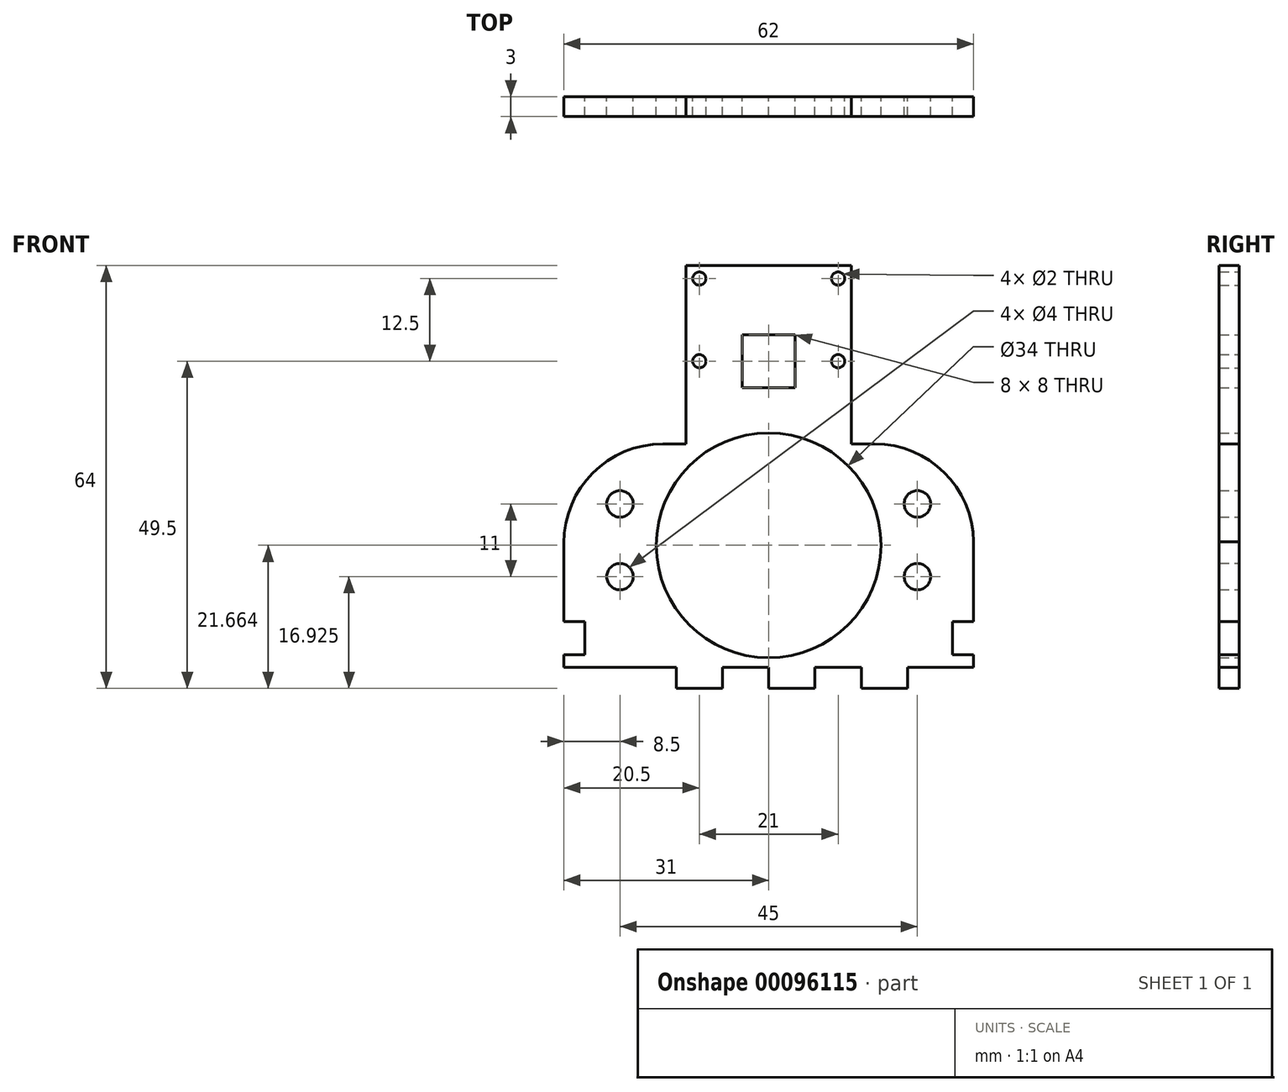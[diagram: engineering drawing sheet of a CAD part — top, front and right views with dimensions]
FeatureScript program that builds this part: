
annotation { "Feature Type Name" : "Feature", "Feature Type Description" : "" }
export const myFeature = defineFeature(function(context is Context, id is Id, definition is map)
    precondition{}
    {
        {
            var Q0;
            Q0=qCreatedBy(makeId("Front.planeOp"),FACE);
            var sketch = newSketch(context, id + "F0", { "sketchPlane" : qUnion([Q0])});
            skLineSegment(sketch, "E0.bottom", {"start": v(12.5, 13.5) * mm, "end": v(-12.5, 13.5) * mm});
            skLineSegment(sketch, "E0.left", {"start": v(12.5, 13.5) * mm, "end": v(12.5, -13.5) * mm});
            skLineSegment(sketch, "E0.right", {"start": v(-12.5, 13.5) * mm, "end": v(-12.5, -13.5) * mm});
            skPoint(sketch, "E0.middle", {"position": v(0, 0) * mm});
            skLineSegment(sketch, "E1", {"start": v(0, 13.5) * mm, "end": v(0, -1) * mm, "construction": true});
            skPoint(sketch, "E1.endSnap0", {"position": v(0, 13.5) * mm});
            skLineSegment(sketch, "E2.bottom", {"start": v(4, 3) * mm, "end": v(-4, 3) * mm});
            skLineSegment(sketch, "E2.top", {"start": v(4, -5) * mm, "end": v(-4, -5) * mm});
            skLineSegment(sketch, "E2.left", {"start": v(4, 3) * mm, "end": v(4, -5) * mm});
            skLineSegment(sketch, "E2.right", {"start": v(-4, 3) * mm, "end": v(-4, -5) * mm});
            skPoint(sketch, "E2.middle", {"position": v(0, -1) * mm});
            skCircle(sketch, "E3", {"center": v(-10.5, 11.5) * mm, "radius": 1 * mm});
            skCircle(sketch, "E4", {"center": v(-10.5, -1) * mm, "radius": 1 * mm});
            skPoint(sketch, "E4.centerSnap0", {"position": v(-4, -1) * mm});
            skCircle(sketch, "E5.MirrorC", {"center": v(10.5, 11.5) * mm, "radius": 1 * mm});
            skCircle(sketch, "E6.MirrorC", {"center": v(10.5, -1) * mm, "radius": 1 * mm});
            skCircle(sketch, "E7", {"center": v(0, -28.84) * mm, "radius": 17 * mm});
            skLineSegment(sketch, "E8", {"start": v(-12.5, -13.5) * mm, "end": v(-16, -13.5) * mm});
            skLineSegment(sketch, "E9", {"start": v(12.5, -13.5) * mm, "end": v(16, -13.5) * mm});
            skArc(sketch, "E10.filletArc", {"start": v(-16, -13.5) * mm, "mid": v(-26.6, -17.9) * mm, "end": v(-31, -28.5) * mm});
            skArc(sketch, "E11.filletArc", {"start": v(31, -28.3) * mm, "mid": v(26.54, -17.82) * mm, "end": v(16, -13.5) * mm});
            skPoint(sketch, "E12.MirrorCS.start.orphan", {"position": v(0, -45.84) * mm});
            skLineSegment(sketch, "E13", {"start": v(-31, -28.5) * mm, "end": v(-31, -35.5) * mm});
            skLineSegment(sketch, "E14", {"start": v(31, -28.3) * mm, "end": v(31, -30.3) * mm});
            skLineSegment(sketch, "E15", {"start": v(0, -28.84) * mm, "end": v(0, -13.5) * mm, "construction": true});
            skLineSegment(sketch, "E16", {"start": v(-31, -30.3) * mm, "end": v(31, -30.3) * mm, "construction": true});
            skLineSegment(sketch, "E17", {"start": v(31, -30.3) * mm, "end": v(31, -35.5) * mm});
            skLineSegment(sketch, "E18", {"start": v(-28, -40.5) * mm, "end": v(28, -40.5) * mm, "construction": true});
            skLineSegment(sketch, "E19", {"start": v(-28, -35.5) * mm, "end": v(28, -35.5) * mm, "construction": true});
            skLineSegment(sketch, "E20", {"start": v(-28, -45.5) * mm, "end": v(28, -45.5) * mm, "construction": true});
            skLineSegment(sketch, "E21.trimOffspring", {"start": v(-31, -35.5) * mm, "end": v(-31, -30.3) * mm, "construction": true});
            skLineSegment(sketch, "E22", {"start": v(31, -47.3) * mm, "end": v(31, -45.4) * mm, "construction": true});
            skLineSegment(sketch, "E23", {"start": v(31, -45.4) * mm, "end": v(27.8, -45.4) * mm});
            skLineSegment(sketch, "E24", {"start": v(27.8, -45.4) * mm, "end": v(27.8, -40.4) * mm});
            skLineSegment(sketch, "E25", {"start": v(27.8, -40.4) * mm, "end": v(31, -40.4) * mm});
            skLineSegment(sketch, "E26", {"start": v(31, -40.4) * mm, "end": v(31, -35.5) * mm});
            skLineSegment(sketch, "E27", {"start": v(-31, -47.3) * mm, "end": v(-31, -45.4) * mm});
            skLineSegment(sketch, "E28", {"start": v(-31, -45.4) * mm, "end": v(-27.8, -45.4) * mm});
            skLineSegment(sketch, "E29", {"start": v(-27.8, -45.4) * mm, "end": v(-27.8, -40.4) * mm});
            skLineSegment(sketch, "E30", {"start": v(-27.8, -40.4) * mm, "end": v(-31, -40.4) * mm});
            skLineSegment(sketch, "E31", {"start": v(-31, -40.4) * mm, "end": v(-31, -35.5) * mm});
            skLineSegment(sketch, "E32", {"start": v(31, -45.4) * mm, "end": v(31, -47.3) * mm});
            skLineSegment(sketch, "E33", {"start": v(0, -22.57) * mm, "end": v(-22.5, -22.57) * mm, "construction": true});
            skLineSegment(sketch, "E34", {"start": v(0, -22.57) * mm, "end": v(22.5, -22.57) * mm, "construction": true});
            skCircle(sketch, "E35", {"center": v(-22.5, -22.57) * mm, "radius": 2 * mm});
            skCircle(sketch, "E36", {"center": v(22.5, -22.57) * mm, "radius": 2 * mm});
            skLineSegment(sketch, "E37", {"start": v(-22.5, -22.57) * mm, "end": v(-22.5, -33.57) * mm, "construction": true});
            skLineSegment(sketch, "E38", {"start": v(22.5, -22.57) * mm, "end": v(22.5, -33.57) * mm, "construction": true});
            skCircle(sketch, "E39", {"center": v(-22.5, -33.57) * mm, "radius": 2 * mm});
            skCircle(sketch, "E40", {"center": v(22.5, -33.57) * mm, "radius": 2 * mm});
            skLineSegment(sketch, "E41", {"start": v(-31, -47.3) * mm, "end": v(-14, -47.3) * mm});
            skLineSegment(sketch, "E42", {"start": v(-14, -47.3) * mm, "end": v(-14, -50.5) * mm});
            skLineSegment(sketch, "E43", {"start": v(-14, -50.5) * mm, "end": v(-7, -50.5) * mm});
            skLineSegment(sketch, "E44", {"start": v(-7, -50.5) * mm, "end": v(-7, -47.3) * mm});
            skLineSegment(sketch, "E45", {"start": v(-7, -47.3) * mm, "end": v(0, -47.3) * mm});
            skLineSegment(sketch, "E46", {"start": v(0, -47.3) * mm, "end": v(0, -50.5) * mm});
            skLineSegment(sketch, "E47", {"start": v(0, -50.5) * mm, "end": v(7, -50.5) * mm});
            skLineSegment(sketch, "E48", {"start": v(7, -50.5) * mm, "end": v(7, -47.3) * mm});
            skLineSegment(sketch, "E49", {"start": v(7, -47.3) * mm, "end": v(14, -47.3) * mm});
            skLineSegment(sketch, "E50", {"start": v(14, -47.3) * mm, "end": v(14, -50.5) * mm});
            skLineSegment(sketch, "E51", {"start": v(14, -50.5) * mm, "end": v(21, -50.5) * mm});
            skLineSegment(sketch, "E52", {"start": v(21, -50.5) * mm, "end": v(21, -47.3) * mm});
            skLineSegment(sketch, "E53", {"start": v(21, -47.3) * mm, "end": v(31, -47.3) * mm});
            skSolve(sketch);
        }
        {
            var Q0;
            Q0 = qSketchRegion(id + "F0", true);
            extrude(context, id + "F1", {"entities" : qUnion([Q0]), "endBound" : BoundingType.SYMMETRIC, "depth" : 3 * mm});
        }
    });
